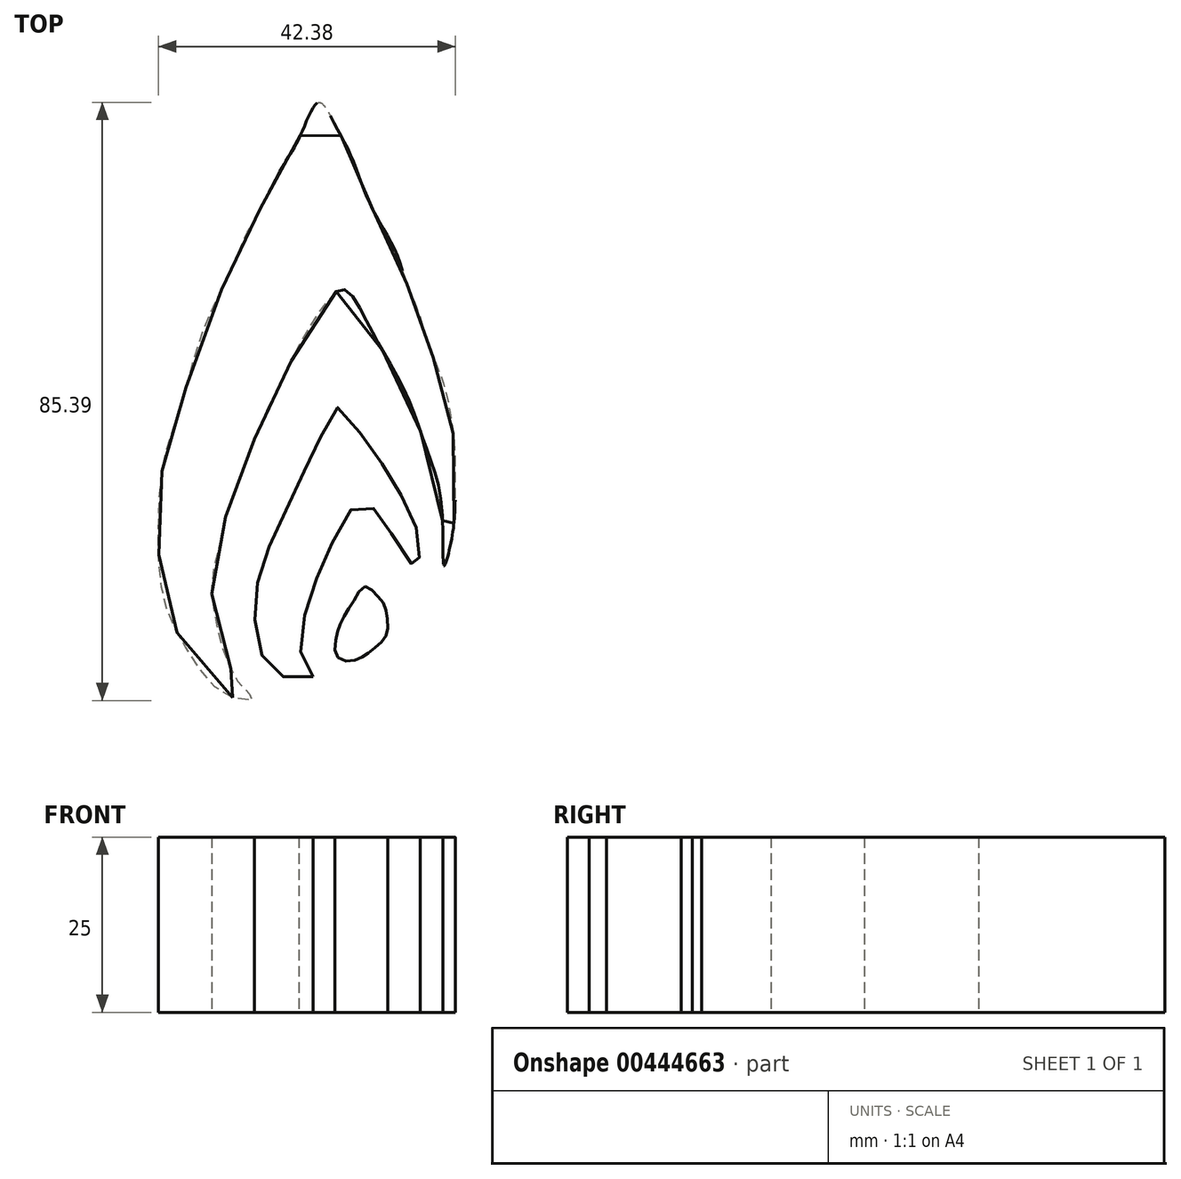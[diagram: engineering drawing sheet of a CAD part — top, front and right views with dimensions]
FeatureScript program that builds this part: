
annotation { "Feature Type Name" : "Feature", "Feature Type Description" : "" }
export const myFeature = defineFeature(function(context is Context, id is Id, definition is map)
    precondition{}
    {
        {
            var Q0;
            Q0=qCreatedBy(makeId("Top.planeOp"),FACE);
            var sketch = newSketch(context, id + "F0", { "sketchPlane" : qUnion([Q0])});
            skFitSpline(sketch, "E0", {"points": [v(23.88, 42.79) * mm, v(20.2, 45.54) * mm, v(16.43, 51.24) * mm, v(14.6, 55.1) * mm, v(13.49, 60.44) * mm, v(13.3, 65.77) * mm, v(13.4, 70.55) * mm, v(14.13, 76.9) * mm, v(15.97, 82.78) * mm, v(17.44, 87.74) * mm, v(20.02, 96.02) * mm, v(23.42, 103.28) * mm, v(25.9, 108.98) * mm, v(28.47, 113.76) * mm, v(31.23, 118.9) * mm, v(33.62, 123.14) * mm, v(36.2, 127.74) * mm, v(38.4, 124.8) * mm, v(40.6, 120.56) * mm, v(42.54, 115.6) * mm, v(44.47, 111.37) * mm, v(47.04, 106.77) * mm, v(48.84, 101.73) * mm, v(50.4, 97.89) * mm, v(51.8, 93.07) * mm, v(53.68, 88.6) * mm, v(54.88, 83.83) * mm, v(55.52, 79.23) * mm, v(55.67, 72.54) * mm, v(55.33, 66.37) * mm, v(54.07, 61.58) * mm, v(53.85, 69) * mm, v(52.48, 75.85) * mm, v(50.65, 80.99) * mm, v(48.37, 86.8) * mm, v(45.4, 92.18) * mm, v(42.89, 96.86) * mm, v(39.69, 101.08) * mm, v(36.5, 98.23) * mm, v(33.75, 93.77) * mm, v(31.47, 89.2) * mm, v(29.3, 84.87) * mm, v(26.44, 78.25) * mm, v(24.16, 72.08) * mm, v(23.02, 69) * mm, v(21.88, 64.09) * mm, v(20.96, 59.75) * mm, v(21.2, 55.3) * mm, v(22.33, 50.16) * mm, v(23.7, 46.73) * mm, v(25.53, 44) * mm, v(27.02, 42.51) * mm, v(23.88, 42.79) * mm]});
            skFitSpline(sketch, "E1", {"points": [v(35.4, 45.74) * mm, v(33.96, 45.5) * mm, v(31.58, 45.62) * mm, v(29.67, 46.57) * mm, v(28.48, 48.24) * mm, v(27.35, 50.15) * mm, v(27.05, 53.49) * mm, v(27.05, 56.4) * mm, v(27.53, 59.45) * mm, v(28.24, 62.07) * mm, v(29.67, 65.53) * mm, v(31.1, 68.63) * mm, v(32.65, 72.2) * mm, v(34.44, 75.72) * mm, v(35.63, 78.47) * mm, v(37.18, 81.03) * mm, v(38.26, 82.7) * mm, v(39.45, 84.78) * mm, v(41.6, 81.33) * mm, v(43.74, 78.47) * mm, v(45.4, 75.84) * mm, v(46.84, 73.52) * mm, v(48.5, 70.72) * mm, v(49.7, 68.21) * mm, v(50.42, 65.95) * mm, v(50.66, 63.8) * mm, v(50.48, 62.07) * mm, v(50.18, 60.22) * mm, v(48.99, 62.85) * mm, v(47.56, 64.7) * mm, v(45.89, 67.26) * mm, v(44.72, 68.82) * mm, v(43.76, 70.17) * mm, v(42.2, 71.43) * mm, v(40.22, 68.5) * mm, v(38.73, 66.18) * mm, v(37.54, 63.32) * mm, v(36.23, 60.52) * mm, v(34.68, 56.88) * mm, v(34.08, 54.2) * mm, v(33.37, 51.16) * mm, v(33.84, 48.6) * mm, v(34.56, 46.93) * mm, v(35.4, 45.74) * mm]});
            skFitSpline(sketch, "E2", {"points": [v(42.8, 58.64) * mm, v(44.3, 57.62) * mm, v(45.5, 56.1) * mm, v(45.96, 54.25) * mm, v(45.96, 52.05) * mm, v(45.23, 50.77) * mm, v(43.56, 49.38) * mm, v(42.25, 48.45) * mm, v(40.4, 48) * mm, v(38.7, 48.84) * mm, v(38.7, 51.24) * mm, v(39.16, 53.02) * mm, v(40.12, 54.95) * mm, v(41.4, 56.96) * mm, v(42.8, 58.64) * mm]});
            skSolve(sketch);
        }
        {
            var Q0;
            Q0 = qSketchRegion(id + "F0", true);
            extrude(context, id + "F1", {"entities" : qUnion([Q0]), "depth" : 25 * mm});
        }
    });
